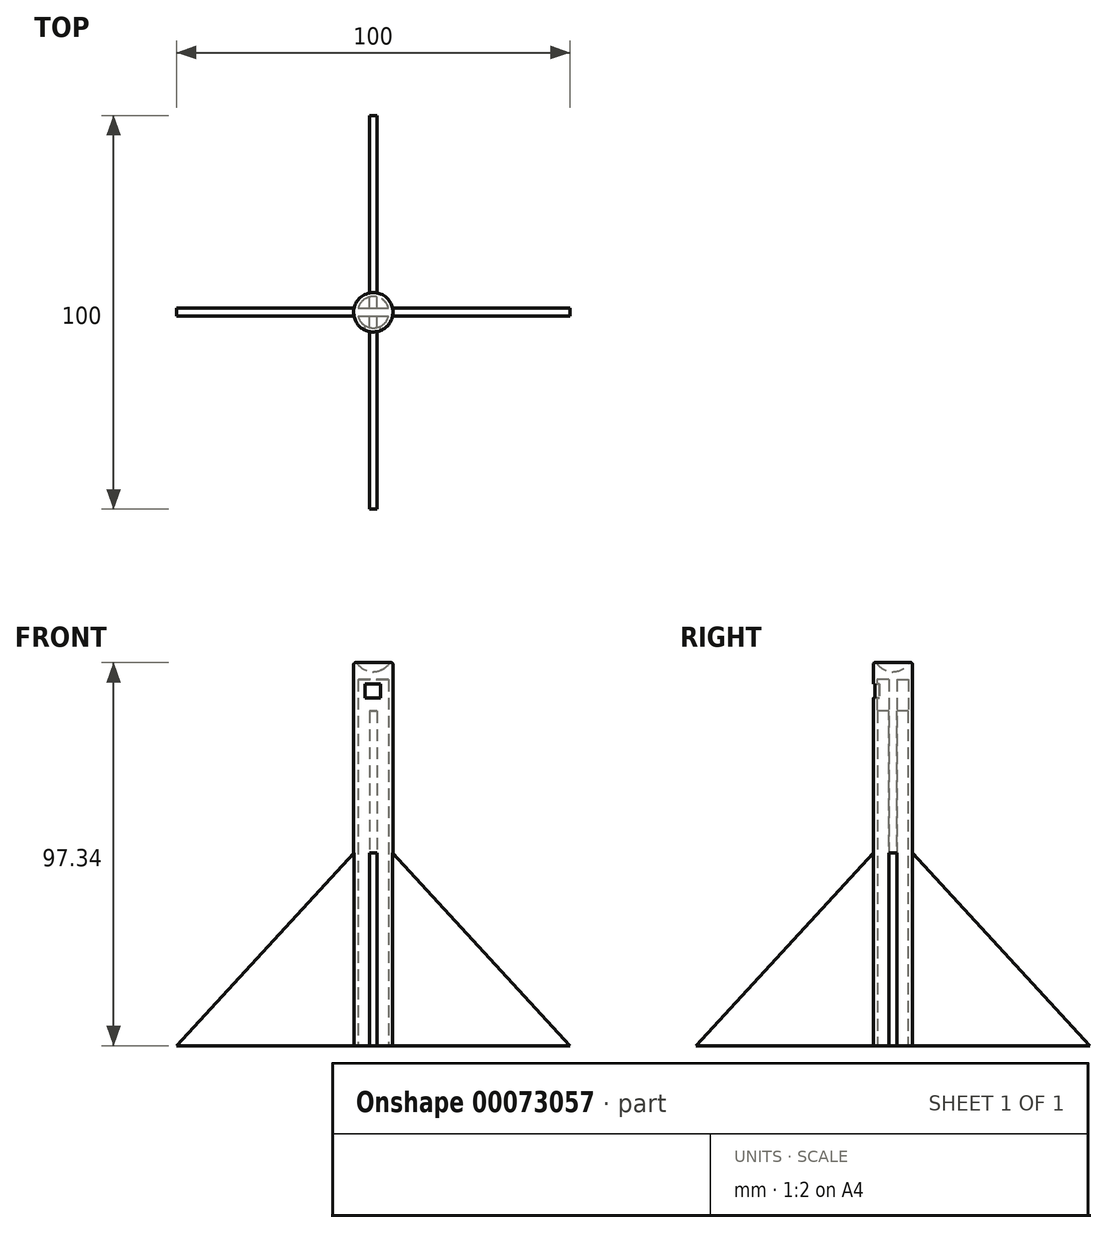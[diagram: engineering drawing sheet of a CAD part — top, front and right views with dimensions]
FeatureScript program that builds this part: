
annotation { "Feature Type Name" : "Feature", "Feature Type Description" : "" }
export const myFeature = defineFeature(function(context is Context, id is Id, definition is map)
    precondition{}
    {
        {
            var Q0;
            Q0=qCreatedBy(makeId("Front.planeOp"),FACE);
            var sketch = newSketch(context, id + "F8", { "sketchPlane" : qUnion([Q0])});
            skArc(sketch, "E0", {"start": v(0, 95) * mm, "mid": v(3.54, 96.46) * mm, "end": v(5, 100) * mm});
            skLineSegment(sketch, "E1", {"start": v(5, 100) * mm, "end": v(5, 0) * mm});
            skLineSegment(sketch, "E2", {"start": v(5, 0) * mm, "end": v(4, 0) * mm});
            skLineSegment(sketch, "E3", {"start": v(4, 0) * mm, "end": v(4, 93) * mm});
            skLineSegment(sketch, "E4", {"start": v(4, 93) * mm, "end": v(0, 93) * mm});
            skLineSegment(sketch, "E5", {"start": v(0, 93) * mm, "end": v(0, 95) * mm});
            skSolve(sketch);
        }
        {
            var Q0;
            Q0=makeQuery(id+"F8.imprint","IMPRINT",FACE,{"disambiguationData":[TD([[makeQuery(id+"F8.imprint","IMPRINT",EDGE,{"derivedFrom":sQuery(id+"F8.wireOp",EDGE,"E0")}),-1.0]])]});
            var Q1;
            Q1=sQuery(id+"F8.wireOp",EDGE,"E5");
            revolve(context, id + "F0", {"entities" : qUnion([Q0]), "axis" : qUnion([Q1]), "revolveType" : RevolveType.FULL});
        }
        {
            var Q0;
            Q0=makeQuery(id+"F0.opRevolve","SWEPT_EDGE",EDGE,{"disambiguationData":[OSD([sQuery(id+"F8.wireOp",EDGE,"E0"),sQuery(id+"F8.wireOp",EDGE,"E1")])]});
            fillet(context, id + "F1", {"entities" : qUnion([Q0]), "radius" : 0.5 * mm, "tangentPropagation" : true, "allowEdgeOverflow" : false});
        }
        {
            var Q0;
            Q0=qCreatedBy(makeId("Front.planeOp"),FACE);
            var sketch = newSketch(context, id + "F2", { "sketchPlane" : qUnion([Q0])});
            skLineSegment(sketch, "E6", {"start": v(50, 0) * mm, "end": v(4, 50) * mm});
            skLineSegment(sketch, "E7", {"start": v(4, 50) * mm, "end": v(4, 95) * mm});
            skLineSegment(sketch, "E8", {"start": v(4, 95) * mm, "end": v(-4, 95) * mm});
            skLineSegment(sketch, "E9", {"start": v(-4, 95) * mm, "end": v(-4, 50) * mm});
            skLineSegment(sketch, "E10", {"start": v(-4, 50) * mm, "end": v(-50, 0) * mm});
            skLineSegment(sketch, "E11", {"start": v(-50, 0) * mm, "end": v(50, 0) * mm});
            skSolve(sketch);
        }
        {
            var Q0;
            Q0=makeQuery(id+"F2.imprint","IMPRINT",FACE,{"disambiguationData":[TD([[makeQuery(id+"F2.imprint","IMPRINT",EDGE,{"derivedFrom":sQuery(id+"F2.wireOp",EDGE,"E6")}),1.0]])]});
            extrude(context, id + "F3", {"entities" : qUnion([Q0]), "operationType" : NewBodyOperationType.ADD, "depth" : 1 * mm, "hasSecondDirection" : true, "secondDirectionOppositeDirection" : true, "secondDirectionDepth" : 1 * mm});
        }
        {
            var Q0;
            Q0=qCreatedBy(makeId("Right.planeOp"),FACE);
            var sketch = newSketch(context, id + "F4", { "sketchPlane" : qUnion([Q0])});
            skLineSegment(sketch, "E12", {"start": v(50, 0) * mm, "end": v(4, 50) * mm});
            skLineSegment(sketch, "E13", {"start": v(4, 50) * mm, "end": v(4, 85) * mm});
            skLineSegment(sketch, "E14", {"start": v(4, 85) * mm, "end": v(-4, 85) * mm});
            skLineSegment(sketch, "E15", {"start": v(-4, 85) * mm, "end": v(-4, 50) * mm});
            skLineSegment(sketch, "E16", {"start": v(-4, 50) * mm, "end": v(-50, 0) * mm});
            skLineSegment(sketch, "E17", {"start": v(-50, 0) * mm, "end": v(50, 0) * mm});
            skSolve(sketch);
        }
        {
            var Q0;
            Q0=makeQuery(id+"F4.imprint","IMPRINT",FACE,{"disambiguationData":[TD([[makeQuery(id+"F4.imprint","IMPRINT",EDGE,{"derivedFrom":sQuery(id+"F4.wireOp",EDGE,"E12")}),1.0]])]});
            extrude(context, id + "F5", {"entities" : qUnion([Q0]), "operationType" : NewBodyOperationType.ADD, "depth" : 1 * mm, "hasSecondDirection" : true, "secondDirectionOppositeDirection" : true, "secondDirectionDepth" : 1 * mm});
        }
        {
            var Q0;
            Q0=qCreatedBy(makeId("Front.planeOp"),FACE);
            var sketch = newSketch(context, id + "F6", { "sketchPlane" : qUnion([Q0])});
            skLineSegment(sketch, "E18.bottom", {"start": v(-2.1, 91.84) * mm, "end": v(1.9, 91.84) * mm});
            skLineSegment(sketch, "E18.top", {"start": v(-2.1, 88.34) * mm, "end": v(1.9, 88.34) * mm});
            skLineSegment(sketch, "E18.left", {"start": v(-2.1, 91.84) * mm, "end": v(-2.1, 88.34) * mm});
            skLineSegment(sketch, "E18.right", {"start": v(1.9, 91.84) * mm, "end": v(1.9, 88.34) * mm});
            skSolve(sketch);
        }
        {
            var Q0;
            Q0 = qSketchRegion(id + "F6", true);
            extrude(context, id + "F7", {"entities" : qUnion([Q0]), "operationType" : NewBodyOperationType.REMOVE, "depth" : 5 * mm, "hasSecondDirection" : true, "secondDirectionOppositeDirection" : false, "secondDirectionDepth" : 1 * mm});
        }
    });
